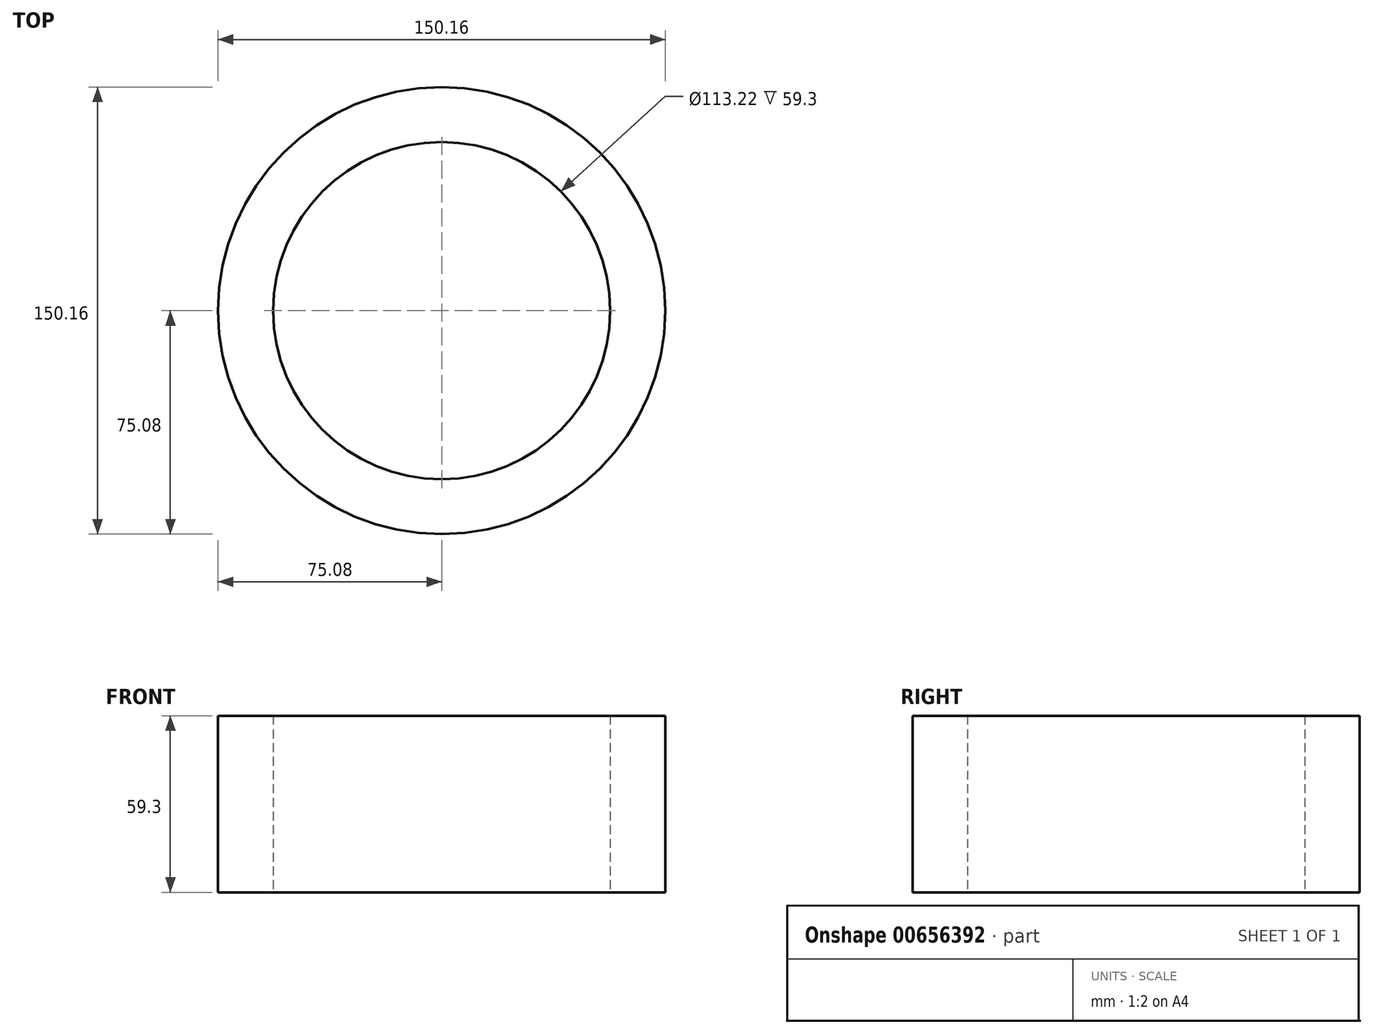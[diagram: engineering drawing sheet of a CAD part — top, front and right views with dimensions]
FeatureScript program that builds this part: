
annotation { "Feature Type Name" : "Feature", "Feature Type Description" : "" }
export const myFeature = defineFeature(function(context is Context, id is Id, definition is map)
    precondition{}
    {
        {
            var Q0;
            Q0=qCreatedBy(makeId("Top.planeOp"),FACE);
            var sketch = newSketch(context, id + "F0", { "sketchPlane" : qUnion([Q0])});
            skCircle(sketch, "E0", {"center": v(0, 0) * mm, "radius": 75.08 * mm});
            skCircle(sketch, "E1", {"center": v(0, 0) * mm, "radius": 56.6 * mm});
            skSolve(sketch);
        }
        {
            var Q0;
            Q0=makeQuery(id+"F0.imprint","IMPRINT",FACE,{"disambiguationData":[TD([[makeQuery(id+"F0.imprint","IMPRINT",EDGE,{"derivedFrom":sQuery(id+"F0.wireOp",EDGE,"E0")}),1.0]])]});
            extrude(context, id + "F1", {"entities" : qUnion([Q0]), "depth" : 59.3 * mm, "offsetDistance" : 25 * mm});
        }
    });
